# Revit family: URA_Eclairage_de_Securite_URALIGHT
name_source: partatom
category: Luminaires
units: mm (PartAtom-declared; Revit-internal decimal feet)

## family parameters
Cote de connecteur circulaire = Utiliser le diamètre
Couper avec des vides une fois chargée = Non
Hôte = Face
Partagée = Non
Point de calcul de pièce = Non
Source d'éclairage = Oui
Type d'élément = Normal

## types (7) — shared parameters
Angle de l'inclinaison = 60.00°
CLASSE_DE_PROTECTION = II
CLASSE_DE_PROTECTION_(IP) = IP42
COULEUR_DU_BOITIER = blanc
Condition Générale d'Utilisation = https://export.legrand.com
DISTANCE_DE_RECONNAISSANCE = 15
DUREE_DE_GARANTIE_BAES_COMPLET = 2
Elévation par défaut = 1219 mm
FORMAT_PRODUIT = rectangle
Fichier de distribution photométrique = generic
Filtre de couleur = 16777215
Gradation des changements de température de couleur de lampe = <Aucun>
MATERIAU_DU_BOITIER = plastique
MATERIAU_DU_COUVERCLE = plastique transparent
TYPE_DE_MONTAGE = pose murale en saillie

## per-type parameters (varying)
| type | ADAPTE_AU_TYPE_DE_MARQUAGE | ALIMENTATION | CATEGORIE_PRODUIT | ETAT_DES_ACCUS | FLUX_LUMINEUX_EN_MODE_D'URGENCE | FONCTION | HAUTEUR/PROFONDEUR | INSTALLATION_DE_SURVEILLANCE | LARGEUR | LONGUEUR | PUISSANCE_DE_LA_LAMPE | REFERENCE_ARTICLE | REF_BATTERIE_DE_RECHANGE | RESERVE_DE_MARCHE | SOURCE_LUMINEUSE | TENSION_NOMINALE_(MAX) | TENSION_NOMINALE_(MIN) | TYPE_DE_COMMUTATION | TYPE_DE_TENSION |
| BAES URALIGHT EVAC CM | autocollant | décentralisé (batterie individuelle) | Autonome | NiCd | 45 | Evac | 70.7 | touche de contrôle | 120 | 258 | 2.7 | 110000 | 186001 | 1 | lampe à incandescence | 253 | 207 | mode veille | CA |
| BAES URALIGHT AMB SATI |  | décentralisé (batterie individuelle) | Autonome | NiCd | 360 | Amb | 74.75 | auto-test automatique | 147.8 | 336 | 8 | 111002 | 186003 | 1 | lampe fluorescente | 253 | 207 | mode veille | CA |
| BAEH URALIGHT CM | autocollant | décentralisé (batterie individuelle) | Autonome | NiCd | 8 | BAEH | 70.7 | touche de contrôle | 120 | 258 | 1.3 | 113000 | 186001 | 5 | lampe à incandescence | 253 | 207 | mode veille | CA |
| LSC AMBIANCE URALIGHT 24 |  | central (batterie centrale) | LSC | non applicable | 360 | Amb | 74.75 | touche de contrôle | 147.8 | 336 | 8 | 241400 |  |  | lampe fluorescente | 24 | 24 | circuit permanent/circuit de secours | CC |
| LSC AMBIANCE URALIGHT 48 |  | central (batterie centrale) | LSC | non applicable | 360 | Amb | 74.75 | touche de contrôle | 147.8 | 336 | 8 | 241410 |  |  | lampe fluorescente | 48 | 48 | circuit permanent/circuit de secours | CC |
| LSC AMBIANCE URALIGHT 110 |  | central (batterie centrale) | LSC | non applicable | 360 | Amb | 74.75 | touche de contrôle | 147.8 | 336 | 8 | 241500 |  |  | lampe fluorescente | 110 | 110 | circuit permanent/circuit de secours | CC |
| LSC AMBIANCE URALIGHT 220/230 |  | central (batterie centrale) | LSC | non applicable | 360 | Amb | 74.75 | touche de contrôle | 147.8 | 336 | 8 | 241510 |  |  | lampe fluorescente | 230 | 220 | circuit permanent/circuit de secours | CA/CC |

note: column(s) folded — value = type name in every type: DESIGNATION_ARTICLE
